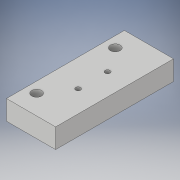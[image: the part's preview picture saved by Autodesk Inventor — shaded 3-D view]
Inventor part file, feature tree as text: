
AUTODESK INVENTOR PART (.ipt)
format: ipt  version: 2017 (Build 210142000, 142)  size: 105,472 bytes
history: native  units: in
note: dims shown in document units (in); Inventor stores cm internally (conversion verified against a paired STEP export)
features: extrude x1, sketch x1
ambient origin geometry x8: Origin, YZ Plane, XZ Plane, XY Plane, X Axis, Y Axis, Z Axis, Center Point
bodies: Solid1 (feature_tree)
feature tree (2):
  extrude  "Extrusion1"  Depth=1.5in
  sketch  "Sketch1"  dims[d0=0.625in d1=1.5in d2=0.303in d3=0.188in d4=0.5in d5=0.125in d7=0.1875in d8=0.063in d9=0.25in d10=0.0in d11=0.276in]
